# Revit family: Reece_Shower_Base_All Directional Shower
name_source: partatom
category: Plumbing Fixtures
revit_build: Autodesk Revit 2018 (Build: 20190510_1515(x64)
units: mm (PartAtom-declared; Revit-internal decimal feet)

## family parameters
Always vertical = Yes
Cut with Voids When Loaded = Yes
Part Type = Normal
Room Calculation Point = Yes
Round Connector Dimension = Use Diameter
Shared = Yes
Work Plane-Based = Yes

## types (1)
- Chrome
    Default Elevation = 0 mm  [stored 0 ft]
    Description = Base All Directional Shower Chrome (3 Star)
    Disclaimer = THIS FILE IS THE PROPERTY OF THE REECE GROUP. IT MAY NOT BE REPRODUCED, REVERSE-ENGINEERED OR MODIFIED. ANY REPUBLICATION, TRANSMISSION OR DISTRIBUTION FOR THE PURPOSE OF COMMERCIALLY EXPLOITING THE FILES IS PROHIBITED.
    Keynote = Product #9504688, Reece_Shower_Base_All Directional Shower - Chrome
    Manufacturer = Base
    Model = -
    Reece_Detail_Disclaimer = THIS FILE IS THE PROPERTY OF THE REECE GROUP. IT MAY NOT BE REPRODUCED, REVERSE-ENGINEERED OR MODIFIED. ANY REPUBLICATION, TRANSMISSION OR DISTRIBUTION FOR THE PURPOSE OF COMMERCIALLY EXPLOITING THE FILES IS PROHIBITED.
    Reece_Detail_Installation = Wall Mounted
    Reece_Material_Colour = Reece_Plastic_ABS
    Reece_Material_Main = Reece_Brass_Chrome
    Reece_Material_Secondary = Reece_Plastic_White
    Reece_Overall_Diameter = 78 mm  [stored 0.255906 ft]
    Reece_Overall_Length = 226 mm  [stored 0.74147 ft]
    Reece_Product_Brand = Base
    Reece_Product_Description = Base All Directional Shower Chrome (3 Star)
    Reece_Product_Mount = Wall Mounted
    Reece_Product_Number = 9504688
    Reece_Product_Sub Brand = -
    Reece_Product_Type = Shower
    Reece_Product_Web Page = www.reece.com.au/product/-9504688
    Reece_Shower_Inlet = 15 mm  [stored 0.0492126 ft]
    Type Comments = Shower
    URL = www.reece.com.au/product/-9504688

note: [stored X ft] marks values corroborated as IEEE doubles in the binary element streams (Revit-internal decimal feet)

## geometry (parser evidence)
native form markers: Sweep x5
no freeform markers — native parametric forms only
